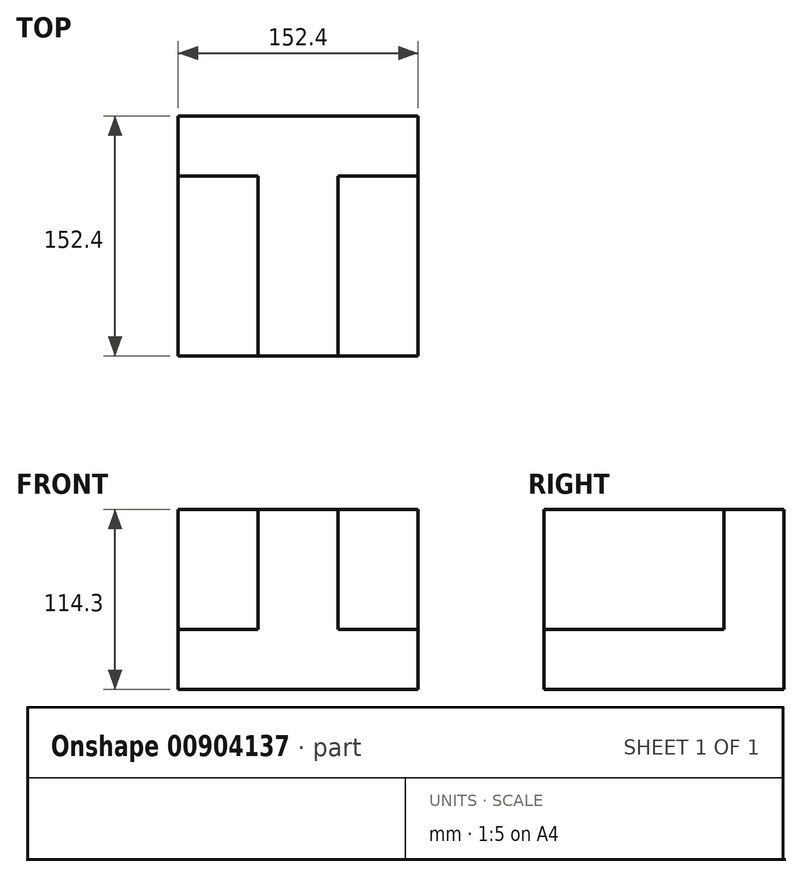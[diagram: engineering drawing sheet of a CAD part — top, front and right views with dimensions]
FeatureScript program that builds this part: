
annotation { "Feature Type Name" : "Feature", "Feature Type Description" : "" }
export const myFeature = defineFeature(function(context is Context, id is Id, definition is map)
    precondition{}
    {
        {
            var Q0;
            Q0=qCreatedBy(makeId("Front.planeOp"),FACE);
            var sketch = newSketch(context, id + "F0", { "sketchPlane" : qUnion([Q0])});
            skLineSegment(sketch, "E0.bottom", {"start": v(-76.2, 57.15) * mm, "end": v(76.2, 57.15) * mm});
            skLineSegment(sketch, "E0.top", {"start": v(-76.2, -57.15) * mm, "end": v(76.2, -57.15) * mm});
            skLineSegment(sketch, "E0.left", {"start": v(-76.2, 57.15) * mm, "end": v(-76.2, -57.15) * mm});
            skLineSegment(sketch, "E0.right", {"start": v(76.2, 57.15) * mm, "end": v(76.2, -57.15) * mm});
            skPoint(sketch, "E0.middle", {"position": v(0, 0) * mm});
            skSolve(sketch);
        }
        {
            var Q0;
            Q0=makeQuery(id+"F0.imprint","IMPRINT",FACE,{"disambiguationData":[TD([[makeQuery(id+"F0.imprint","IMPRINT",EDGE,{"derivedFrom":sQuery(id+"F0.wireOp",EDGE,"E0.bottom")}),-1.0]])]});
            extrude(context, id + "F1", {"entities" : qUnion([Q0]), "depth" : 152.4 * mm, "offsetDistance" : 25.4 * mm});
        }
        {
            var Q0;
            Q0=makeQuery(id+"F1.opExtrude","CAP_FACE",FACE,{"disambiguationData":[OSD([sQuery(id+"F0.wireOp",EDGE,"E0.bottom"),sQuery(id+"F0.wireOp",EDGE,"E0.top"),sQuery(id+"F0.wireOp",EDGE,"E0.left"),sQuery(id+"F0.wireOp",EDGE,"E0.right")])],"isStart":false});
            var sketch = newSketch(context, id + "F2", { "sketchPlane" : qUnion([Q0])});
            skLineSegment(sketch, "E1", {"start": v(-76.2, -57.15) * mm, "end": v(-76.2, -19.05) * mm});
            skLineSegment(sketch, "E2", {"start": v(-76.2, -19.05) * mm, "end": v(-25.4, -19.05) * mm});
            skLineSegment(sketch, "E3", {"start": v(-25.4, -19.05) * mm, "end": v(-25.4, 57.15) * mm});
            skLineSegment(sketch, "E4", {"start": v(-25.4, 57.15) * mm, "end": v(25.4, 57.15) * mm});
            skLineSegment(sketch, "E5", {"start": v(25.4, 57.15) * mm, "end": v(25.4, -19.05) * mm});
            skLineSegment(sketch, "E6", {"start": v(25.4, -19.05) * mm, "end": v(76.2, -19.05) * mm});
            skLineSegment(sketch, "E7", {"start": v(76.2, -19.05) * mm, "end": v(76.2, -57.15) * mm});
            skSolve(sketch);
        }
        {
            var Q0;
            {var subQ0=sQuery(id+"F2.wireOp",EDGE,"E2");Q0=makeQuery(id+"F2.imprint","IMPRINT",FACE,{"disambiguationData":[TD([[makeQuery(id+"F2.imprint","IMPRINT",EDGE,{"derivedFrom":subQ0}),1.0]])]});}
            extrude(context, id + "F3", {"entities" : qUnion([Q0]), "operationType" : NewBodyOperationType.REMOVE, "oppositeDirection" : true, "depth" : 114.3 * mm, "offsetDistance" : 25.4 * mm});
        }
        {
            var Q0;
            {var subQ0=sQuery(id+"F2.wireOp",EDGE,"E5");Q0=makeQuery(id+"F2.imprint","IMPRINT",FACE,{"disambiguationData":[TD([[makeQuery(id+"F2.imprint","IMPRINT",EDGE,{"derivedFrom":subQ0}),1.0]])]});}
            extrude(context, id + "F4", {"entities" : qUnion([Q0]), "operationType" : NewBodyOperationType.REMOVE, "oppositeDirection" : true, "depth" : 114.3 * mm, "offsetDistance" : 25.4 * mm});
        }
    });
